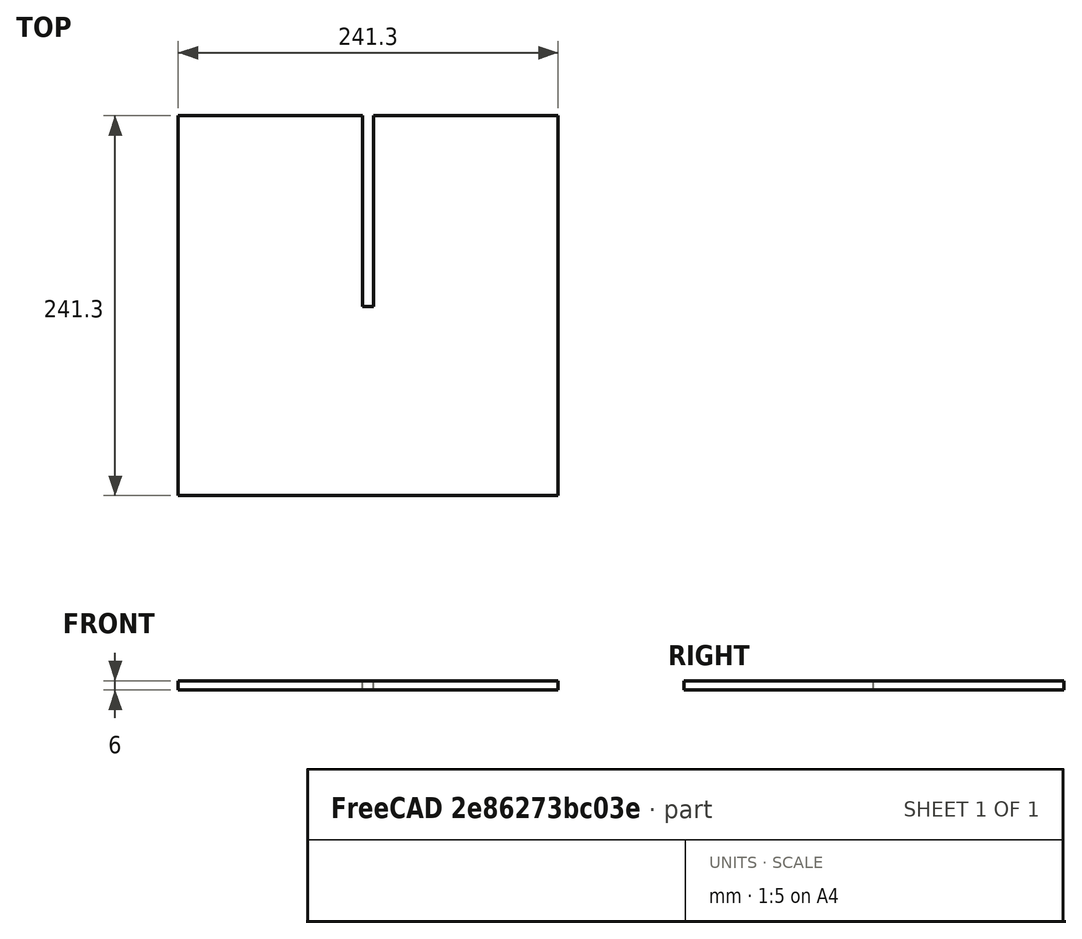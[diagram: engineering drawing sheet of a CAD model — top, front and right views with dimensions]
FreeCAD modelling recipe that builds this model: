
FCSTD DOCUMENT  (FreeCAD 0.21R33675 (Git))
Label: box_divider
License: All rights reserved
LicenseURL: https://en.wikipedia.org/wiki/All_rights_reserved
objects: Spreadsheet::Sheet×1, Sketcher::SketchObject×1, PartDesign::Pad×1, PartDesign::Body×1
note: 4 computed .brp shape members not serialized (recipe doc carries the construction recipe); baked Part::Feature solids carry a one-line shape summary decoded from their .brp

FEATURE [Spreadsheet::Sheet] Spreadsheet
  cells = A2='Design Parameters; A3='width; B3(width)==9.5 in; A4='height; B4(height)==9.5 in; A5='thickness; B5(thickness)==6 mm; A7='slot_width_margin; B7(slot_width_margin)==0.5 mm; A8='slot_depth_margin; B8(slot_depth_margin)==0.5 mm; A9='slot_width; B9(slot_width)==thickness + 2 * slot_width_margin; A10='slot_depth; B10(slot_depth)==0.5 * height + slot_depth_margin
FEATURE [Sketcher::SketchObject] Sketch
  FullyConstrained = true
  MapMode = 5
  Support = -> [XY_Plane]
  expr: Constraints[10] = Spreadsheet.height
  expr: Constraints[11] = Spreadsheet.width
  expr: Constraints[24] = Spreadsheet.slot_width
  expr: Constraints[25] = Spreadsheet.slot_depth
  sketch-geometry (10):
    g0: LineSegment StartX=-120.65 StartY=120.65 StartZ=0 EndX=-120.65 EndY=-120.65 EndZ=0
    g1: LineSegment StartX=-120.65 StartY=-120.65 StartZ=0 EndX=120.65 EndY=-120.65 EndZ=0
    g2: LineSegment StartX=120.65 StartY=-120.65 StartZ=0 EndX=120.65 EndY=120.65 EndZ=0
    g3: LineSegment StartX=120.65 StartY=120.65 StartZ=0 EndX=-120.65 EndY=120.65 EndZ=0
    g4: GeomPoint X=0 Y=0 Z=0
    g5: LineSegment StartX=-120.65 StartY=120.65 StartZ=0 EndX=-3.5 EndY=120.65 EndZ=0
    g6: LineSegment StartX=120.65 StartY=120.65 StartZ=0 EndX=3.5 EndY=120.65 EndZ=0
    g7: LineSegment StartX=-3.5 StartY=120.65 StartZ=0 EndX=-3.5 EndY=-0.5 EndZ=0
    g8: LineSegment StartX=-3.5 StartY=-0.5 StartZ=0 EndX=3.5 EndY=-0.5 EndZ=0
    g9: LineSegment StartX=3.5 StartY=-0.5 StartZ=0 EndX=3.5 EndY=120.65 EndZ=0
  constraints (26):
    c: Coincident(g0,g1)
    c: Coincident(g1,g2)
    c: Coincident(g2,g3)
    c: Coincident(g3,g0)
    c: Horizontal(g1)
    c: Horizontal(g3)
    c: Vertical(g0)
    c: Vertical(g2)
    c: Symmetric(g1,g0,g4)
    c: Coincident(g4,g-1)
    c: DistanceY(g2,g2) = 241.3
    c: DistanceX(g1,g1) = 241.3
    c: Coincident(g5,g0)
    c: PointOnObject(g5,g3)
    c: Coincident(g6,g2)
    c: PointOnObject(g6,g3)
    c: Equal(g5,g6)
    c: Coincident(g7,g8)
    c: Coincident(g8,g9)
    c: Vertical(g7)
    c: Vertical(g9)
    c: Horizontal(g8)
    c: Coincident(g7,g5)
    c: Coincident(g9,g6)
    c: DistanceX(g8,g8) = 7
    c: DistanceY(g9,g9) = 121.15
FEATURE [PartDesign::Pad] Pad
  Direction = (0,0,1)
  Length = 6
  Length2 = 10
  Profile = -> Sketch
  ReferenceAxis = -> Sketch [N_Axis]
  Type = 0
  expr: Length = Spreadsheet.thickness
FEATURE [PartDesign::Body] Body
  Group = -> [Sketch,Pad]
  Origin = -> Origin
  Tip = -> Pad
